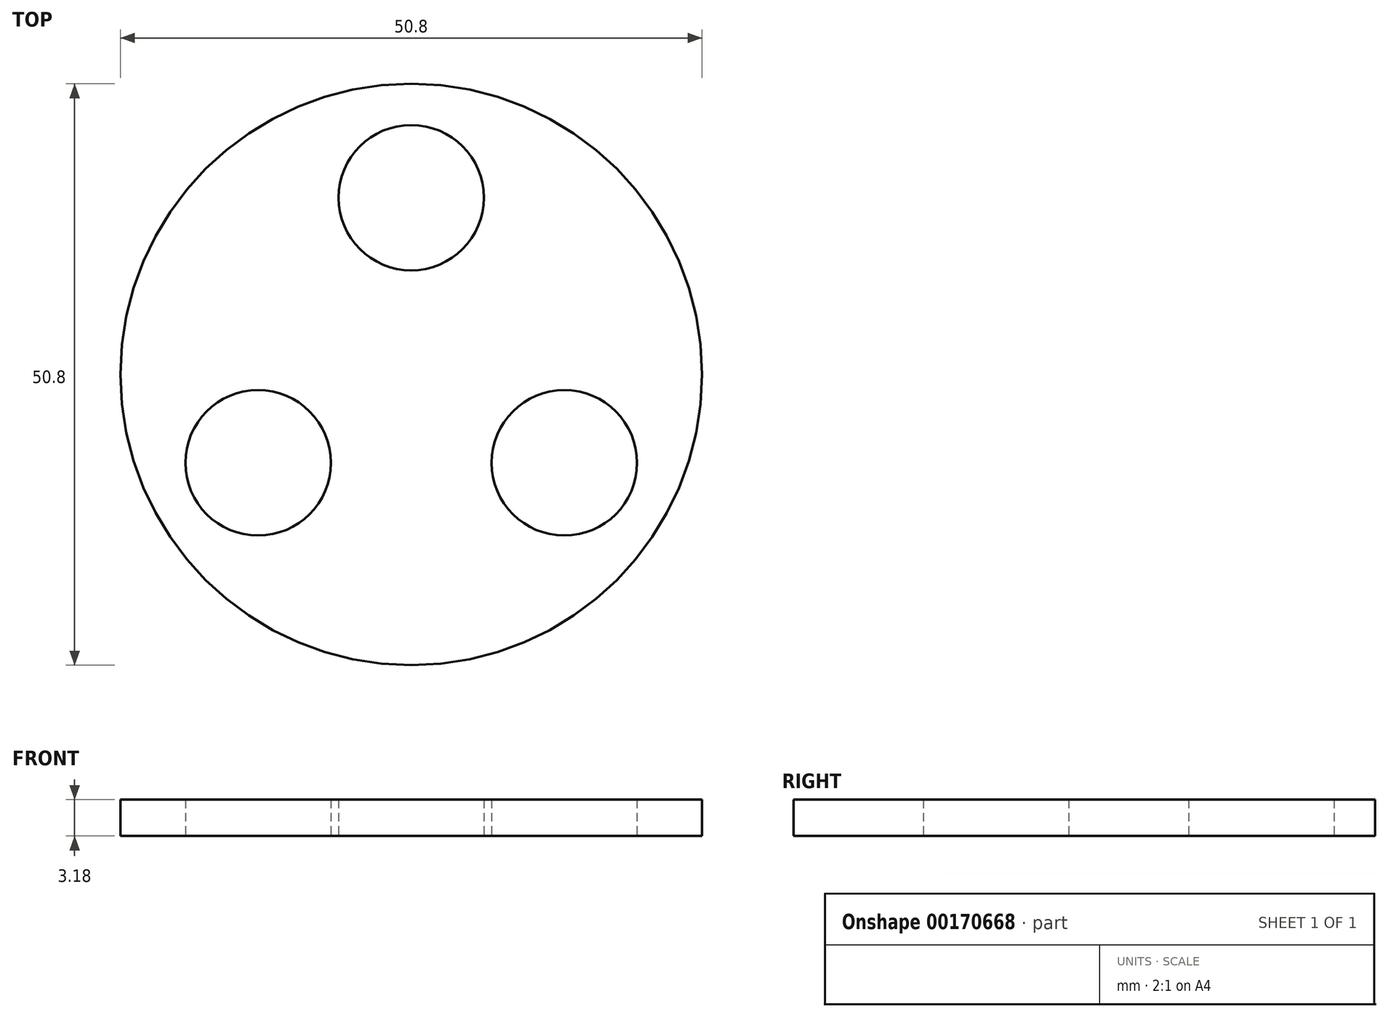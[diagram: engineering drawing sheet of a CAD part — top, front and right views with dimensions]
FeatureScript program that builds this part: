
annotation { "Feature Type Name" : "Feature", "Feature Type Description" : "" }
export const myFeature = defineFeature(function(context is Context, id is Id, definition is map)
    precondition{}
    {
        {
            var Q0;
            Q0=qCreatedBy(makeId("Top.planeOp"),FACE);
            var sketch = newSketch(context, id + "F0", { "sketchPlane" : qUnion([Q0])});
            skCircle(sketch, "E0", {"center": v(0, 0) * mm, "radius": 25.4 * mm});
            skSolve(sketch);
        }
        {
            var Q0;
            Q0 = qSketchRegion(id + "F0", true);
            extrude(context, id + "F1", {"entities" : qUnion([Q0]), "depth" : 3.17 * mm});
        }
        {
            var Q0;
            Q0=qCreatedBy(makeId("Top.planeOp"),FACE);
            var sketch = newSketch(context, id + "F2", { "sketchPlane" : qUnion([Q0])});
            skCircle(sketch, "E1", {"center": v(0, 15.45) * mm, "radius": 6.35 * mm});
            skCircle(sketch, "E2.1.0", {"center": v(-13.38, -7.72) * mm, "radius": 6.35 * mm});
            skCircle(sketch, "E2.2.0", {"center": v(13.38, -7.72) * mm, "radius": 6.35 * mm});
            skPoint(sketch, "E2.center", {"position": v(0, 0) * mm});
            skSolve(sketch);
        }
        {
            var Q0;
            Q0 = qSketchRegion(id + "F2", true);
            extrude(context, id + "F3", {"entities" : qUnion([Q0]), "endBound" : BoundingType.UP_TO_NEXT, "depth" : 6.35 * mm});
        }
    });
